# Revit family: Anti_Siphon_Sillcock-Box_Type-JayR.Smith-557X_Series
name_source: partatom
category: Plumbing Fixtures
units: mm (PartAtom-declared; Revit-internal decimal feet)

## family parameters
Cut with Voids When Loaded = Yes
Host = Face
OmniClass Number = 23.45.55.14
OmniClass Title = Single Faucets
Part Type = Normal
Room Calculation Point = No
Round Connector Dimension = Use Diameter
Shared = No

## types (2) — shared parameters
-BFP Dual Check Valve = No
-CL Cylinder Lock = No
-TAP (2) 3/8" Tappings = No
Assembly Code = D2020300
Body Material = Metal-JayR.Smith-Cast Brass
Box Material = Stainless Steel-JayR.Smith-Grey
CW Connection = Yes
Default Elevation = 0"
Description = Mild Climate, Anti-Siphon Sillcock and Stainless Steel Box
HW Connection = No
Handle Material = Aluminum-JayR.Smith-Powder Coated
Height = 4"
Height- Box = 11"
Height- Wall Opening = 9 3/4"
Hose Connection  Size = 3/4"
Hose Connection Description = 3/4" Hose Outlet Connection
Inlet Size = 1"
Installation Type = Wall Mounted
Length = 3"
Manufacturer = JayR.Smith
Operator Type = Handle
Product Documentation Link = https://www.jrsmith.com
Product Page URL = https://www.jrsmith.com
URL = https://www.jrsmith.com
Vent Connection = No
Waste Connection = No
Width = 2"
Width- Box = 7 1/8"
Width- Wall Opening = 6"

## per-type parameters (varying)
| type | Connection Description | Inlet Radius |
| 5572 | 1/2" Female NPT Inlet Connection | 1/4" |
| 5573 | 3/4" Female NPT Inlet Connection | 3/8" |

note: column(s) folded — value = type name in every type: Model

## geometry (parser evidence)
native form markers: Sweep x1
no freeform markers — native parametric forms only
